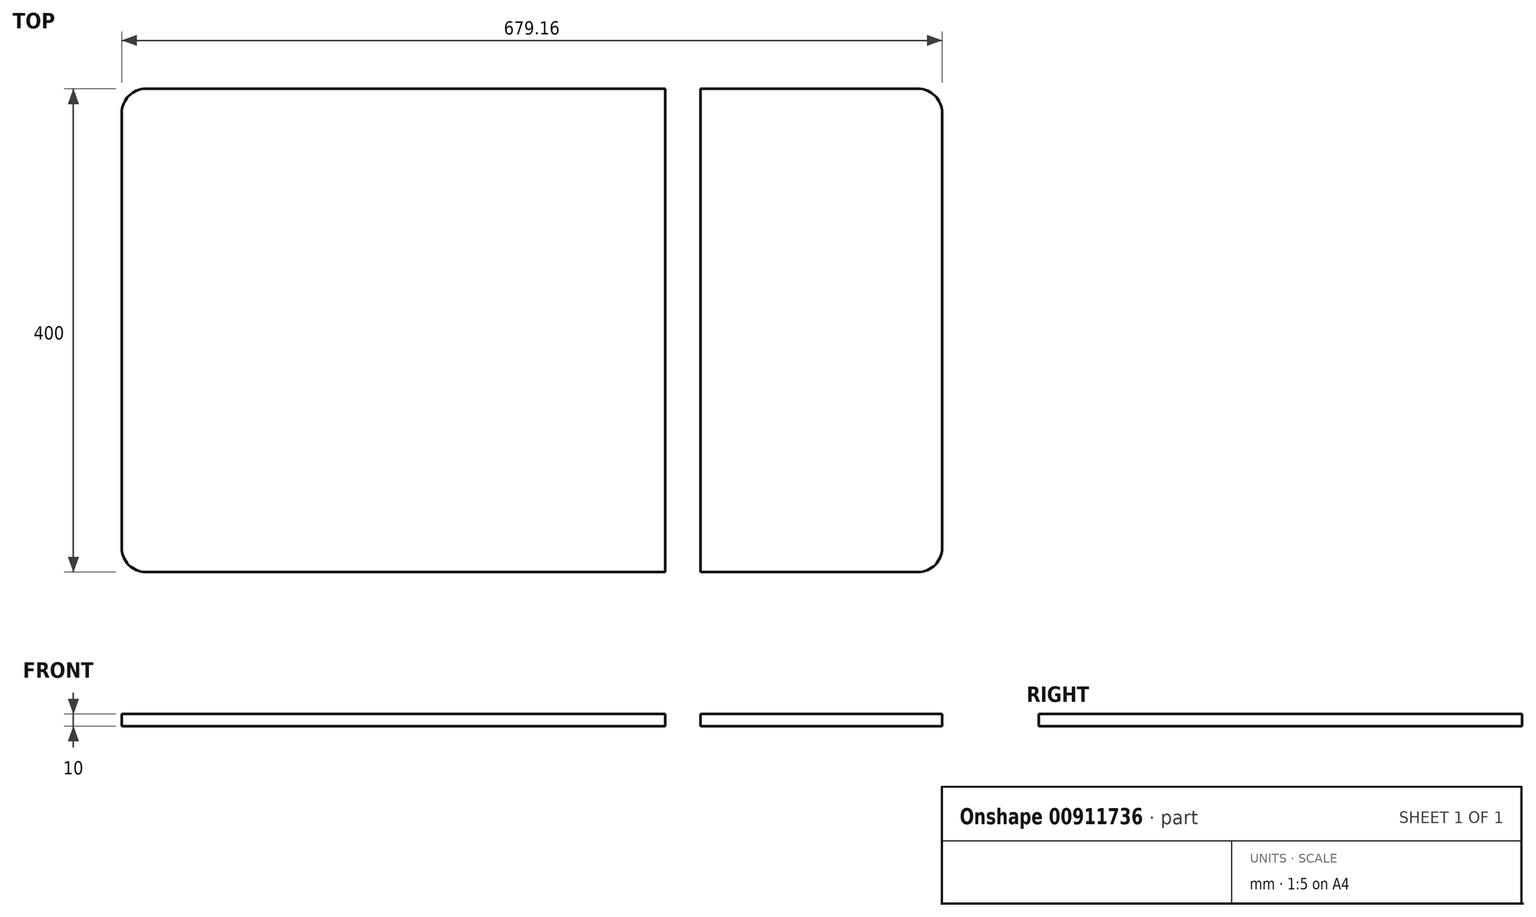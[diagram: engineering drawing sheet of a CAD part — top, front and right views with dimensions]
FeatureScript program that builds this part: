
annotation { "Feature Type Name" : "Feature", "Feature Type Description" : "" }
export const myFeature = defineFeature(function(context is Context, id is Id, definition is map)
    precondition{}
    {
        {
            var Q0;
            Q0=qCreatedBy(makeId("Top.planeOp"),FACE);
            var sketch = newSketch(context, id + "F0", { "sketchPlane" : qUnion([Q0])});
            skLineSegment(sketch, "E0.bottom", {"start": v(0, 0) * mm, "end": v(-430, 0) * mm});
            skLineSegment(sketch, "E0.top", {"start": v(0, 400) * mm, "end": v(-430, 400) * mm});
            skLineSegment(sketch, "E0.left", {"start": v(0, 0) * mm, "end": v(0, 400) * mm});
            skLineSegment(sketch, "E0.right", {"start": v(-450, 20) * mm, "end": v(-450, 380) * mm});
            skPoint(sketch, "E1.visualSharp", {"position": v(-450, 400) * mm});
            skArc(sketch, "E1.filletArc", {"start": v(-430, 400) * mm, "mid": v(-444.14, 394.14) * mm, "end": v(-450, 380) * mm});
            skPoint(sketch, "E2.visualSharp", {"position": v(-450, 0) * mm});
            skArc(sketch, "E2.filletArc", {"start": v(-450, 20) * mm, "mid": v(-444.14, 5.86) * mm, "end": v(-430, 0) * mm});
            skSolve(sketch);
        }
        {
            var Q0;
            Q0 = qSketchRegion(id + "F0", true);
            extrude(context, id + "F1", {"entities" : qUnion([Q0]), "depth" : 10 * mm, "offsetDistance" : 25 * mm});
        }
        {
            var Q0;
            Q0=qCreatedBy(makeId("Top.planeOp"),FACE);
            var sketch = newSketch(context, id + "F2", { "sketchPlane" : qUnion([Q0])});
            skLineSegment(sketch, "E3.bottom", {"start": v(29.16, 0) * mm, "end": v(209.16, 0) * mm});
            skLineSegment(sketch, "E3.top", {"start": v(29.16, 400) * mm, "end": v(209.16, 400) * mm});
            skLineSegment(sketch, "E3.left", {"start": v(29.16, 0) * mm, "end": v(29.16, 400) * mm});
            skLineSegment(sketch, "E3.right", {"start": v(229.16, 20) * mm, "end": v(229.16, 380) * mm});
            skPoint(sketch, "E4.visualSharp", {"position": v(229.16, 400) * mm});
            skArc(sketch, "E4.filletArc", {"start": v(229.16, 380) * mm, "mid": v(223.3, 394.14) * mm, "end": v(209.16, 400) * mm});
            skPoint(sketch, "E5.visualSharp", {"position": v(229.16, 0) * mm});
            skArc(sketch, "E5.filletArc", {"start": v(209.16, 0) * mm, "mid": v(223.3, 5.86) * mm, "end": v(229.16, 20) * mm});
            skSolve(sketch);
        }
        {
            var Q0;
            Q0=makeQuery(id+"F2.imprint","IMPRINT",FACE,{"disambiguationData":[TD([[makeQuery(id+"F2.imprint","IMPRINT",EDGE,{"derivedFrom":sQuery(id+"F2.wireOp",EDGE,"E3.bottom")}),1.0]])]});
            extrude(context, id + "F3", {"entities" : qUnion([Q0]), "depth" : 10 * mm, "offsetDistance" : 25 * mm});
        }
    });
